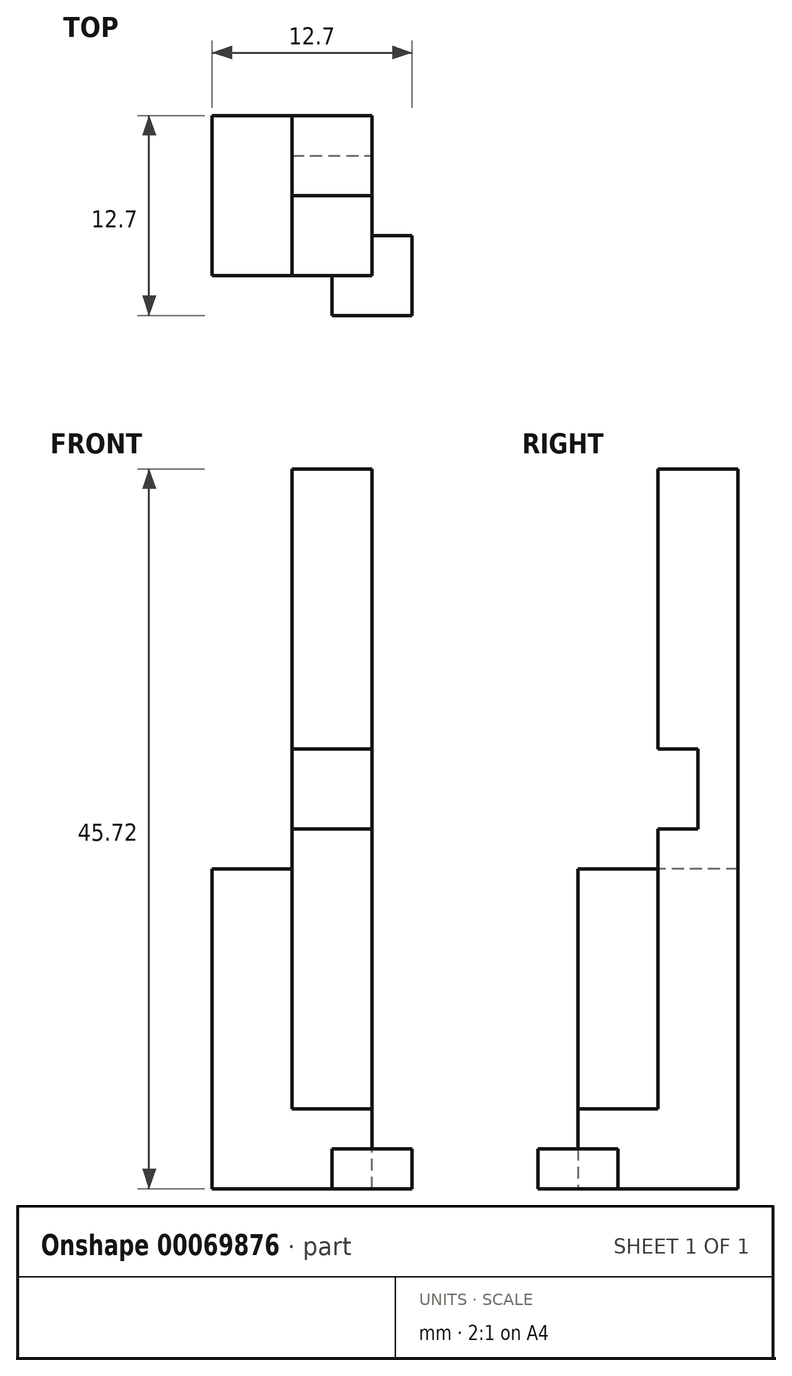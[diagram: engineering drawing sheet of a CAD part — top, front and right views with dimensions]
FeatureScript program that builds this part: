
annotation { "Feature Type Name" : "Feature", "Feature Type Description" : "" }
export const myFeature = defineFeature(function(context is Context, id is Id, definition is map)
    precondition{}
    {
        {
            var Q0;
            Q0=qCreatedBy(makeId("Top.planeOp"),FACE);
            var sketch = newSketch(context, id + "F0", { "sketchPlane" : qUnion([Q0])});
            skLineSegment(sketch, "E0.bottom", {"start": v(0, 0) * mm, "end": v(10.16, 0) * mm});
            skLineSegment(sketch, "E0.top", {"start": v(0, -10.16) * mm, "end": v(10.16, -10.16) * mm});
            skLineSegment(sketch, "E0.left", {"start": v(0, 0) * mm, "end": v(0, -10.16) * mm});
            skLineSegment(sketch, "E0.right", {"start": v(10.16, 0) * mm, "end": v(10.16, -10.16) * mm});
            skSolve(sketch);
        }
        {
            var Q0;
            Q0=qSketchRegion(id+"F0",true);
            extrude(context, id + "F1", {"entities" : qUnion([Q0]), "depth" : 5.08 * mm});
        }
        {
            var Q0;
            Q0=makeQuery(id+"F1.opExtrude","CAP_FACE",FACE,{"disambiguationData":[OSD([sQuery(id+"F0.wireOp",EDGE,"E0.bottom"),sQuery(id+"F0.wireOp",EDGE,"E0.top"),sQuery(id+"F0.wireOp",EDGE,"E0.left"),sQuery(id+"F0.wireOp",EDGE,"E0.right")])],"isStart":true});
            var sketch = newSketch(context, id + "F2", { "sketchPlane" : qUnion([Q0])});
            skLineSegment(sketch, "E1.bottom", {"start": v(7.62, 7.62) * mm, "end": v(12.7, 7.62) * mm});
            skLineSegment(sketch, "E1.top", {"start": v(7.62, 12.7) * mm, "end": v(12.7, 12.7) * mm});
            skLineSegment(sketch, "E1.left", {"start": v(7.62, 7.62) * mm, "end": v(7.62, 12.7) * mm});
            skLineSegment(sketch, "E1.right", {"start": v(12.7, 7.62) * mm, "end": v(12.7, 12.7) * mm});
            skSolve(sketch);
        }
        {
            var Q0;
            Q0=qSketchRegion(id+"F2",true);
            extrude(context, id + "F3", {"entities" : qUnion([Q0]), "operationType" : NewBodyOperationType.ADD, "oppositeDirection" : true, "depth" : 2.54 * mm});
        }
        {
            var Q0;
            Q0=makeQuery(id+"F1.opExtrude","CAP_FACE",FACE,{"disambiguationData":[OSD([sQuery(id+"F0.wireOp",EDGE,"E0.bottom"),sQuery(id+"F0.wireOp",EDGE,"E0.top"),sQuery(id+"F0.wireOp",EDGE,"E0.left"),sQuery(id+"F0.wireOp",EDGE,"E0.right")])],"isStart":false});
            var sketch = newSketch(context, id + "F4", { "sketchPlane" : qUnion([Q0])});
            skLineSegment(sketch, "E2.bottom", {"start": v(10.16, 0) * mm, "end": v(5.08, 0) * mm});
            skLineSegment(sketch, "E2.top", {"start": v(10.16, -5.08) * mm, "end": v(5.08, -5.08) * mm});
            skLineSegment(sketch, "E2.left", {"start": v(10.16, 0) * mm, "end": v(10.16, -5.08) * mm});
            skLineSegment(sketch, "E2.right", {"start": v(5.08, 0) * mm, "end": v(5.08, -5.08) * mm});
            skSolve(sketch);
        }
        {
            var Q0;
            Q0=qSketchRegion(id+"F4",true);
            extrude(context, id + "F5", {"entities" : qUnion([Q0]), "operationType" : NewBodyOperationType.ADD, "depth" : 40.64 * mm});
        }
        {
            var Q0;
            Q0=makeQuery(id+"F5.boolean.opBoolean","MERGE",FACE,{"derivedFrom":[makeQuery(id+"F1.opExtrude","SWEPT_FACE",FACE,{"disambiguationData":[OSD([sQuery(id+"F0.wireOp",EDGE,"E0.right")])]}),makeQuery(id+"F5.opExtrude","SWEPT_FACE",FACE,{"disambiguationData":[OSD([sQuery(id+"F4.wireOp",EDGE,"E2.left")])]})]});
            var sketch = newSketch(context, id + "F6", { "sketchPlane" : qUnion([Q0])});
            skLineSegment(sketch, "E3.bottom", {"start": v(-2.54, 22.86) * mm, "end": v(-7.62, 22.86) * mm});
            skLineSegment(sketch, "E3.top", {"start": v(-2.54, 27.94) * mm, "end": v(-7.62, 27.94) * mm});
            skLineSegment(sketch, "E3.left", {"start": v(-2.54, 22.86) * mm, "end": v(-2.54, 27.94) * mm});
            skLineSegment(sketch, "E3.right", {"start": v(-7.62, 22.86) * mm, "end": v(-7.62, 27.94) * mm});
            skSolve(sketch);
        }
        {
            var Q0;
            Q0=qSketchRegion(id+"F6",true);
            extrude(context, id + "F7", {"entities" : qUnion([Q0]), "operationType" : NewBodyOperationType.REMOVE, "oppositeDirection" : true, "depth" : 25.4 * mm});
        }
        {
            var Q0;
            Q0=makeQuery(id+"F1.opExtrude","CAP_FACE",FACE,{"disambiguationData":[OSD([sQuery(id+"F0.wireOp",EDGE,"E0.bottom"),sQuery(id+"F0.wireOp",EDGE,"E0.top"),sQuery(id+"F0.wireOp",EDGE,"E0.left"),sQuery(id+"F0.wireOp",EDGE,"E0.right")])],"isStart":false});
            var sketch = newSketch(context, id + "F8", { "sketchPlane" : qUnion([Q0])});
            skLineSegment(sketch, "E4.bottom", {"start": v(5.08, 0) * mm, "end": v(0, 0) * mm});
            skLineSegment(sketch, "E4.top", {"start": v(5.08, -10.16) * mm, "end": v(0, -10.16) * mm});
            skLineSegment(sketch, "E4.left", {"start": v(5.08, 0) * mm, "end": v(5.08, -10.16) * mm});
            skLineSegment(sketch, "E4.right", {"start": v(0, 0) * mm, "end": v(0, -10.16) * mm});
            skSolve(sketch);
        }
        {
            var Q0;
            Q0 = qSketchRegion(id + "F8", true);
            extrude(context, id + "F9", {"entities" : qUnion([Q0]), "operationType" : NewBodyOperationType.ADD, "depth" : 15.24 * mm});
        }
    });
